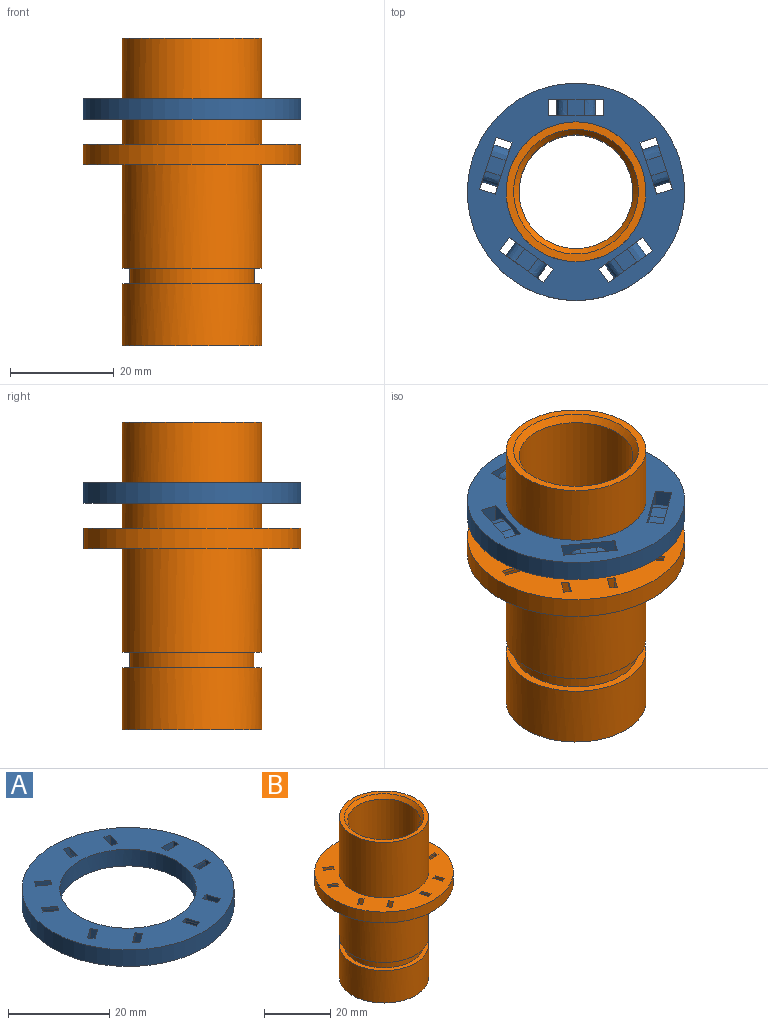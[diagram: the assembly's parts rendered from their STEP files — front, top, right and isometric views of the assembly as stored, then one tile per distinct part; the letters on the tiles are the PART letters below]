
ASSEMBLY  parts=2 mates=1
PART A: 49 faces, bbox 42.2x42.2x4.2 mm
  f0: plane 42x42mm, normal (0,0,-1), area 645.1mm2, adj f2,f3,f4,f6,f7,f9,f10,f12
  f1: plane 42x42mm, normal (0,0,1), area 765.3mm2, adj f2,f3,f4,f6,f7,f9,f10,f12
  f2: cylinder r=21mm len=42mm, axis (0,0,-1), area 527.8mm2, adj f0,f1
  f3: plane 10.2x4.23mm, normal (0.31,0.95,0), area 22.5mm2, adj f0,f1,f5,f22,f23,f30,f31,f44
  f4: plane 10.2x4.23mm, normal (-0.31,-0.95,0), area 22.5mm2, adj f0,f1,f5,f22,f23,f30,f31,f44
  f5: plane 4.01x3.95mm, normal (0,0,-1), area 10mm2, adj f3,f4,f44,f45
  f6: plane 8.71x6.39mm, normal (-0.81,0.59,0), area 22.5mm2, adj f0,f1,f8,f32,f33,f34,f35,f42
  f7: plane 8.71x6.39mm, normal (0.81,-0.59,0), area 22.5mm2, adj f0,f1,f8,f32,f33,f34,f35,f42
  f8: plane 4.42x4.4mm, normal (0,0,-1), area 10mm2, adj f6,f7,f42,f43
  f9: plane 8.71x6.39mm, normal (-0.81,-0.59,0), area 22.5mm2, adj f0,f1,f11,f20,f21,f36,f37,f40
  f10: plane 8.71x6.39mm, normal (0.81,0.59,0), area 22.5mm2, adj f0,f1,f11,f20,f21,f36,f37,f40
  f11: plane 4.42x4.4mm, normal (0,0,-1), area 10mm2, adj f9,f10,f40,f41
  f12: plane 10.2x4.23mm, normal (0.31,-0.95,0), area 22.5mm2, adj f0,f1,f14,f24,f25,f26,f27,f38
  f13: plane 10.2x4.23mm, normal (-0.31,0.95,0), area 22.5mm2, adj f0,f1,f14,f24,f25,f26,f27,f38
  f14: plane 4.01x3.95mm, normal (0,0,-1), area 10mm2, adj f12,f13,f38,f39
  f15: plane 10.71x4.23mm, normal (-1,0,0), area 22.5mm2, adj f0,f1,f17,f18,f19,f28,f29,f46
  f16: plane 10.71x4.23mm, normal (1,0,0), area 22.5mm2, adj f0,f1,f17,f18,f19,f28,f29,f46
  f17: plane 3.2x3.11mm, normal (0,0,-1), area 10mm2, adj f15,f16,f46,f47
  f18: plane 3.2x0.6mm, normal (0,-1,0), area 1.9mm2, adj f1,f15,f16,f47
  f19: plane 4x3.2mm, normal (0,1,0), area 12.8mm2, adj f0,f1,f15,f16
  f20: plane 4x2.59mm, normal (-0.59,0.81,0), area 12.8mm2, adj f0,f1,f9,f10
  f21: plane 2.59x1.88mm, normal (0.59,-0.81,0), area 1.9mm2, adj f1,f9,f10,f40
  f22: plane 4x3.04mm, normal (-0.95,0.31,0), area 12.8mm2, adj f0,f1,f3,f4
  f23: plane 3.04x0.99mm, normal (0.95,-0.31,0), area 1.9mm2, adj f1,f3,f4,f45
  f24: plane 4x3.04mm, normal (-0.95,-0.31,0), area 12.8mm2, adj f0,f1,f12,f13
  f25: plane 3.04x0.99mm, normal (0.95,0.31,0), area 1.9mm2, adj f1,f12,f13,f38
  f26: plane 4x3.04mm, normal (0.95,0.31,0), area 12.8mm2, adj f0,f1,f12,f13
  f27: plane 3.04x0.99mm, normal (-0.95,-0.31,0), area 1.9mm2, adj f1,f12,f13,f39
  f28: plane 4x3.2mm, normal (0,-1,0), area 12.8mm2, adj f0,f1,f15,f16
  f29: plane 3.2x0.6mm, normal (0,1,0), area 1.9mm2, adj f1,f15,f16,f46
  f30: plane 4x3.04mm, normal (0.95,-0.31,0), area 12.8mm2, adj f0,f1,f3,f4
  f31: plane 3.04x0.99mm, normal (-0.95,0.31,0), area 1.9mm2, adj f1,f3,f4,f44
  f32: plane 4x2.59mm, normal (-0.59,-0.81,0), area 12.8mm2, adj f0,f1,f6,f7
  f33: plane 2.59x1.88mm, normal (0.59,0.81,0), area 1.9mm2, adj f1,f6,f7,f43
  f34: plane 4x2.59mm, normal (0.59,0.81,0), area 12.8mm2, adj f0,f1,f6,f7
  f35: plane 2.59x1.88mm, normal (-0.59,-0.81,0), area 1.9mm2, adj f1,f6,f7,f42
  f36: plane 4x2.59mm, normal (0.59,-0.81,0), area 12.8mm2, adj f0,f1,f9,f10
  f37: plane 2.59x1.88mm, normal (-0.59,0.81,0), area 1.9mm2, adj f1,f9,f10,f41
  f38: bspline ~4.03x3.18mm, area 11.4mm2, adj f12,f13,f14,f25
  f39: bspline ~4.03x3.18mm, area 11.4mm2, adj f12,f13,f14,f27
  f40: bspline ~4.14x3.85mm, area 11.4mm2, adj f9,f10,f11,f21
  f41: bspline ~3.88x3.66mm, area 11.4mm2, adj f9,f10,f11,f37
  f42: bspline ~3.88x3.66mm, area 11.4mm2, adj f6,f7,f8,f35
  f43: bspline ~4.14x3.85mm, area 11.4mm2, adj f6,f7,f8,f33
  f44: bspline ~4.03x3.18mm, area 11.4mm2, adj f3,f4,f5,f31
  f45: bspline ~4.03x3.18mm, area 11.4mm2, adj f3,f4,f5,f23
  f46: bspline ~3.52x2.2mm, area 11.4mm2, adj f15,f16,f17,f29
  f47: bspline ~3.52x2.2mm, area 11.4mm2, adj f15,f16,f17,f18
  f48: cylinder r=13.5mm len=27mm, axis (0,0,1), area 339.3mm2, adj f0,f1
PART B: 58 faces, bbox 42.2x42.2x59.7 mm
  f0: cylinder r=13.5mm len=27mm, axis (0,0,1), area 1017.9mm2, adj f54,f55
  f1: plane 42x42mm, normal (0,0,-1), area 645.1mm2, adj f6,f7,f8,f10,f11,f13,f14,f16
  f2: plane 42x42mm, normal (0,0,1), area 765.3mm2, adj f3,f6,f7,f8,f10,f11,f13,f14
  f3: cylinder r=13.5mm len=27mm, axis (0,0,-1), area 1738.9mm2, adj f2,f5
  f4: cylinder r=11mm len=58.25mm, axis (0,0,-1), area 4026mm2, adj f52,f54
  f5: plane 27x27mm, normal (0,0,1), area 116.5mm2, adj f3,f52
  f6: cylinder r=21mm len=42mm, axis (0,0,-1), area 527.8mm2, adj f1,f2
  f7: plane 10.2x4.23mm, normal (0.31,0.95,0), area 22.5mm2, adj f1,f2,f9,f26,f27,f34,f35,f48
  f8: plane 10.2x4.23mm, normal (-0.31,-0.95,0), area 22.5mm2, adj f1,f2,f9,f26,f27,f34,f35,f48
  f9: plane 4.01x3.95mm, normal (0,0,-1), area 10mm2, adj f7,f8,f48,f49
  f10: plane 8.71x6.39mm, normal (-0.81,0.59,0), area 22.5mm2, adj f1,f2,f12,f36,f37,f38,f39,f46
  f11: plane 8.71x6.39mm, normal (0.81,-0.59,0), area 22.5mm2, adj f1,f2,f12,f36,f37,f38,f39,f46
  f12: plane 4.42x4.4mm, normal (0,0,-1), area 10mm2, adj f10,f11,f46,f47
  f13: plane 8.71x6.39mm, normal (-0.81,-0.59,0), area 22.5mm2, adj f1,f2,f15,f24,f25,f40,f41,f44
  f14: plane 8.71x6.39mm, normal (0.81,0.59,0), area 22.5mm2, adj f1,f2,f15,f24,f25,f40,f41,f44
  f15: plane 4.42x4.4mm, normal (0,0,-1), area 10mm2, adj f13,f14,f44,f45
  f16: plane 10.2x4.23mm, normal (0.31,-0.95,0), area 22.5mm2, adj f1,f2,f18,f28,f29,f30,f31,f42
  f17: plane 10.2x4.23mm, normal (-0.31,0.95,0), area 22.5mm2, adj f1,f2,f18,f28,f29,f30,f31,f42
  f18: plane 4.01x3.95mm, normal (0,0,-1), area 10mm2, adj f16,f17,f42,f43
  f19: plane 10.71x4.23mm, normal (-1,0,0), area 22.5mm2, adj f1,f2,f21,f22,f23,f32,f33,f50
  f20: plane 10.71x4.23mm, normal (1,0,0), area 22.5mm2, adj f1,f2,f21,f22,f23,f32,f33,f50
  f21: plane 3.2x3.11mm, normal (0,0,-1), area 10mm2, adj f19,f20,f50,f51
  f22: plane 3.2x0.6mm, normal (0,-1,0), area 1.9mm2, adj f2,f19,f20,f51
  f23: plane 4x3.2mm, normal (0,1,0), area 12.8mm2, adj f1,f2,f19,f20
  f24: plane 4x2.59mm, normal (-0.59,0.81,0), area 12.8mm2, adj f1,f2,f13,f14
  f25: plane 2.59x1.88mm, normal (0.59,-0.81,0), area 1.9mm2, adj f2,f13,f14,f44
  f26: plane 4x3.04mm, normal (-0.95,0.31,0), area 12.8mm2, adj f1,f2,f7,f8
  f27: plane 3.04x0.99mm, normal (0.95,-0.31,0), area 1.9mm2, adj f2,f7,f8,f49
  f28: plane 4x3.04mm, normal (-0.95,-0.31,0), area 12.8mm2, adj f1,f2,f16,f17
  f29: plane 3.04x0.99mm, normal (0.95,0.31,0), area 1.9mm2, adj f2,f16,f17,f42
  f30: plane 4x3.04mm, normal (0.95,0.31,0), area 12.8mm2, adj f1,f2,f16,f17
  f31: plane 3.04x0.99mm, normal (-0.95,-0.31,0), area 1.9mm2, adj f2,f16,f17,f43
  f32: plane 4x3.2mm, normal (0,-1,0), area 12.8mm2, adj f1,f2,f19,f20
  f33: plane 3.2x0.6mm, normal (0,1,0), area 1.9mm2, adj f2,f19,f20,f50
  f34: plane 4x3.04mm, normal (0.95,-0.31,0), area 12.8mm2, adj f1,f2,f7,f8
  f35: plane 3.04x0.99mm, normal (-0.95,0.31,0), area 1.9mm2, adj f2,f7,f8,f48
  f36: plane 4x2.59mm, normal (-0.59,-0.81,0), area 12.8mm2, adj f1,f2,f10,f11
  f37: plane 2.59x1.88mm, normal (0.59,0.81,0), area 1.9mm2, adj f2,f10,f11,f47
  f38: plane 4x2.59mm, normal (0.59,0.81,0), area 12.8mm2, adj f1,f2,f10,f11
  f39: plane 2.59x1.88mm, normal (-0.59,-0.81,0), area 1.9mm2, adj f2,f10,f11,f46
  f40: plane 4x2.59mm, normal (0.59,-0.81,0), area 12.8mm2, adj f1,f2,f13,f14
  f41: plane 2.59x1.88mm, normal (-0.59,0.81,0), area 1.9mm2, adj f2,f13,f14,f45
  f42: bspline ~4.03x3.18mm, area 11.4mm2, adj f16,f17,f18,f29
  f43: bspline ~4.03x3.18mm, area 11.4mm2, adj f16,f17,f18,f31
  f44: bspline ~4.14x3.85mm, area 11.4mm2, adj f13,f14,f15,f25
  f45: bspline ~3.88x3.66mm, area 11.4mm2, adj f13,f14,f15,f41
  f46: bspline ~3.88x3.66mm, area 11.4mm2, adj f10,f11,f12,f39
  f47: bspline ~4.14x3.85mm, area 11.4mm2, adj f10,f11,f12,f37
  f48: bspline ~4.03x3.18mm, area 11.4mm2, adj f7,f8,f9,f35
  f49: bspline ~4.03x3.18mm, area 11.4mm2, adj f7,f8,f9,f27
  f50: bspline ~3.52x2.2mm, area 11.4mm2, adj f19,f20,f21,f33
  f51: bspline ~3.52x2.2mm, area 11.4mm2, adj f19,f20,f21,f22
  f52: cone r=11mm half-angle=40deg, axis (0,0,1), area 118.2mm2, adj f4,f5
  f53: cylinder r=13.5mm len=27mm, axis (0,0,1), area 1696.5mm2, adj f1,f57
  f54: plane 27x27mm, normal (0,0,-1), area 192.4mm2, adj f0,f4
  f55: plane 27x27mm, normal (0,0,1), area 120.2mm2, adj f0,f56
  f56: cylinder r=12mm len=24mm, axis (0,0,-1), area 226.2mm2, adj f55,f57
  f57: plane 27x27mm, normal (0,0,-1), area 120.2mm2, adj f53,f56
PLACE A rot(axis=(-0.71,-0.71,0),180deg) t=(0,0,47.77)mm
PLACE B rot(axis=(0,0,1),90deg) t=(0,0,35)mm
MATE slider A.f2 <-> B.f0  axis (0,0,1) through (0,0,43.77)mm
